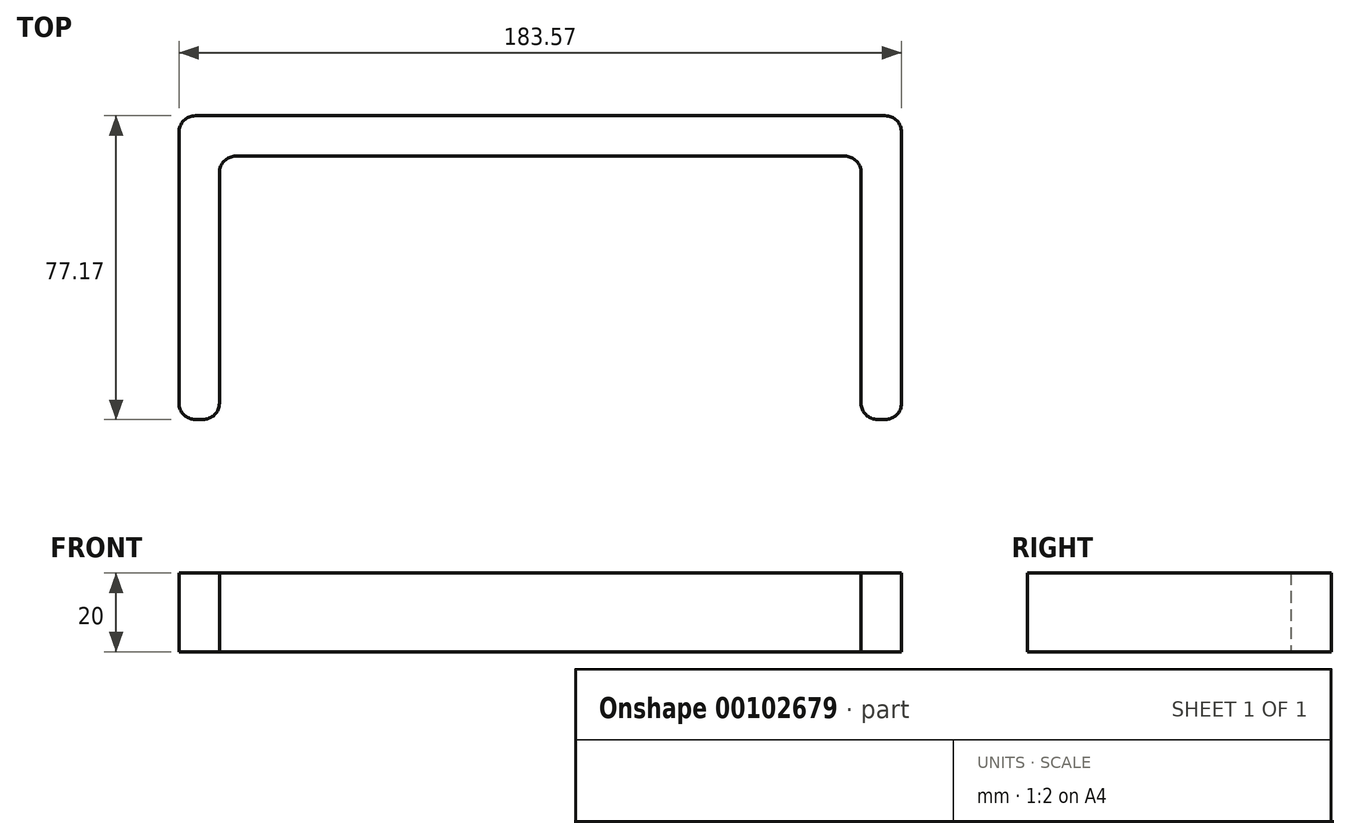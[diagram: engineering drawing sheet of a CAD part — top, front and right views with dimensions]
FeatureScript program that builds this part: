
annotation { "Feature Type Name" : "Feature", "Feature Type Description" : "" }
export const myFeature = defineFeature(function(context is Context, id is Id, definition is map)
    precondition{}
    {
        {
            var Q0;
            Q0=qCreatedBy(makeId("Top.planeOp"),FACE);
            var sketch = newSketch(context, id + "F0", { "sketchPlane" : qUnion([Q0])});
            skLineSegment(sketch, "E0.bottom", {"start": v(-111.15, 52.8) * mm, "end": v(43.54, 52.8) * mm});
            skLineSegment(sketch, "E0.left", {"start": v(-115.32, 48.63) * mm, "end": v(-115.32, -9.93) * mm});
            skLineSegment(sketch, "E0.right", {"start": v(47.71, 48.63) * mm, "end": v(47.71, -9.93) * mm});
            skLineSegment(sketch, "E1.0", {"start": v(-125.6, 58.9) * mm, "end": v(-125.6, -9.93) * mm});
            skLineSegment(sketch, "E1.1", {"start": v(-121.42, 63.07) * mm, "end": v(53.8, 63.07) * mm});
            skLineSegment(sketch, "E1.2", {"start": v(57.98, 58.9) * mm, "end": v(57.98, -9.93) * mm});
            skLineSegment(sketch, "E2", {"start": v(-121.42, -14.1) * mm, "end": v(-119.5, -14.1) * mm});
            skLineSegment(sketch, "E3", {"start": v(51.89, -14.1) * mm, "end": v(53.8, -14.1) * mm});
            skPoint(sketch, "E4.visualSharp", {"position": v(-115.32, -14.1) * mm});
            skArc(sketch, "E4.filletArc", {"start": v(-119.5, -14.1) * mm, "mid": v(-116.55, -12.88) * mm, "end": v(-115.32, -9.93) * mm});
            skPoint(sketch, "E5.visualSharp", {"position": v(-125.6, -14.1) * mm});
            skArc(sketch, "E5.filletArc", {"start": v(-125.6, -9.93) * mm, "mid": v(-124.37, -12.88) * mm, "end": v(-121.42, -14.1) * mm});
            skPoint(sketch, "E6.visualSharp", {"position": v(-125.6, 63.07) * mm});
            skArc(sketch, "E6.filletArc", {"start": v(-121.42, 63.07) * mm, "mid": v(-124.37, 61.84) * mm, "end": v(-125.6, 58.9) * mm});
            skPoint(sketch, "E7.visualSharp", {"position": v(-115.32, 52.8) * mm});
            skArc(sketch, "E7.filletArc", {"start": v(-111.15, 52.8) * mm, "mid": v(-114.1, 51.58) * mm, "end": v(-115.32, 48.63) * mm});
            skPoint(sketch, "E8.visualSharp", {"position": v(47.71, 52.8) * mm});
            skArc(sketch, "E8.filletArc", {"start": v(47.71, 48.63) * mm, "mid": v(46.5, 51.58) * mm, "end": v(43.54, 52.8) * mm});
            skPoint(sketch, "E9.visualSharp", {"position": v(57.98, 63.07) * mm});
            skArc(sketch, "E9.filletArc", {"start": v(57.98, 58.9) * mm, "mid": v(56.76, 61.84) * mm, "end": v(53.8, 63.07) * mm});
            skPoint(sketch, "E10.visualSharp", {"position": v(57.98, -14.1) * mm});
            skArc(sketch, "E10.filletArc", {"start": v(53.8, -14.1) * mm, "mid": v(56.76, -12.88) * mm, "end": v(57.98, -9.93) * mm});
            skPoint(sketch, "E11.visualSharp", {"position": v(47.71, -14.1) * mm});
            skArc(sketch, "E11.filletArc", {"start": v(47.71, -9.93) * mm, "mid": v(48.94, -12.88) * mm, "end": v(51.89, -14.1) * mm});
            skSolve(sketch);
        }
        {
            var Q0;
            Q0=makeQuery(id+"F0.imprint","IMPRINT",FACE,{"disambiguationData":[TD([[makeQuery(id+"F0.imprint","IMPRINT",EDGE,{"derivedFrom":sQuery(id+"F0.wireOp",EDGE,"E0.bottom")}),1.0]])]});
            extrude(context, id + "F1", {"entities" : qUnion([Q0]), "depth" : 20 * mm});
        }
    });
